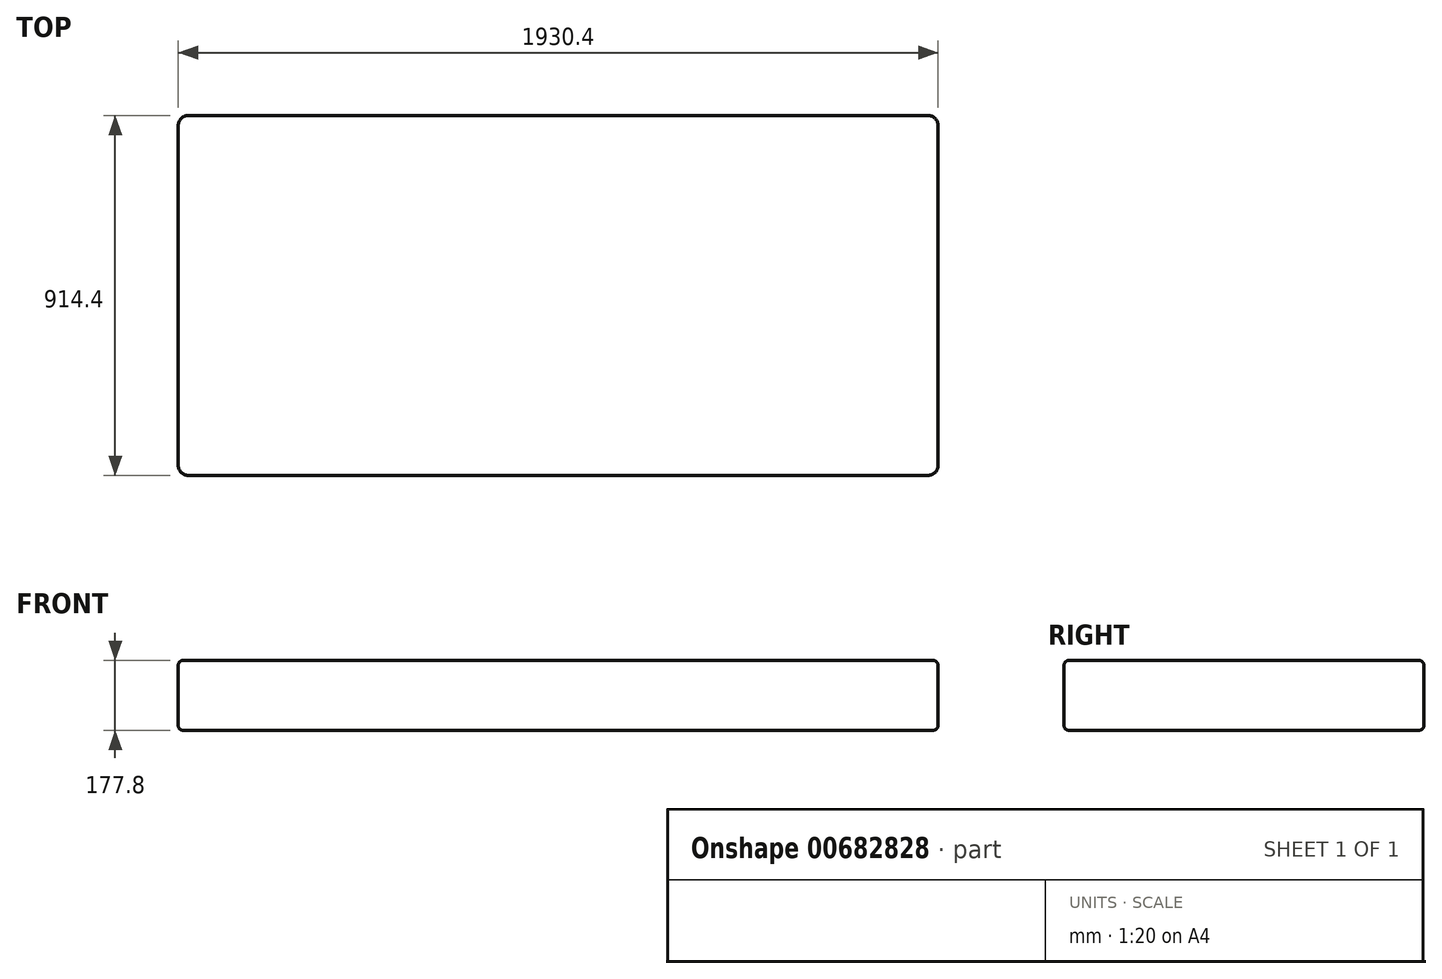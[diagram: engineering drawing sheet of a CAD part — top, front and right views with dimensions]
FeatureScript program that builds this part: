
annotation { "Feature Type Name" : "Feature", "Feature Type Description" : "" }
export const myFeature = defineFeature(function(context is Context, id is Id, definition is map)
    precondition{}
    {
        {
            var Q0;
            Q0=qCreatedBy(makeId("Top.planeOp"),FACE);
            var sketch = newSketch(context, id + "F0", { "sketchPlane" : qUnion([Q0])});
            skLineSegment(sketch, "E0.bottom", {"start": v(0, 0) * mm, "end": v(-1930.4, 0) * mm});
            skLineSegment(sketch, "E0.top", {"start": v(0, 914.4) * mm, "end": v(-1930.4, 914.4) * mm});
            skLineSegment(sketch, "E0.left", {"start": v(0, 0) * mm, "end": v(0, 914.4) * mm});
            skLineSegment(sketch, "E0.right", {"start": v(-1930.4, 0) * mm, "end": v(-1930.4, 914.4) * mm});
            skSolve(sketch);
        }
        {
            var Q0;
            Q0=makeQuery(id+"F0.imprint","IMPRINT",FACE,{"disambiguationData":[TD([[makeQuery(id+"F0.imprint","IMPRINT",EDGE,{"derivedFrom":sQuery(id+"F0.wireOp",EDGE,"E0.bottom")}),-1.0]])]});
            extrude(context, id + "F1", {"entities" : qUnion([Q0]), "depth" : 177.8 * mm, "offsetDistance" : 25.4 * mm});
        }
        {
            var Q0;
            Q0=makeQuery(id+"F1.opExtrude","CAP_FACE",FACE,{"disambiguationData":[OSD([sQuery(id+"F0.wireOp",EDGE,"E0.bottom"),sQuery(id+"F0.wireOp",EDGE,"E0.top"),sQuery(id+"F0.wireOp",EDGE,"E0.left"),sQuery(id+"F0.wireOp",EDGE,"E0.right")])],"isStart":false});
            fillet(context, id + "F2", {"entities" : qUnion([Q0]), "radius" : 12.7 * mm, "tangentPropagation" : true, "allowEdgeOverflow" : false});
        }
        {
            var Q0;
            Q0=makeQuery(id+"F1.opExtrude","CAP_FACE",FACE,{"disambiguationData":[OSD([sQuery(id+"F0.wireOp",EDGE,"E0.bottom"),sQuery(id+"F0.wireOp",EDGE,"E0.top"),sQuery(id+"F0.wireOp",EDGE,"E0.left"),sQuery(id+"F0.wireOp",EDGE,"E0.right")])],"isStart":true});
            fillet(context, id + "F3", {"entities" : qUnion([Q0]), "radius" : 12.7 * mm, "tangentPropagation" : true, "allowEdgeOverflow" : false});
        }
        {
            var Q0;
            Q0=makeQuery(id+"F1.opExtrude","SWEPT_EDGE",EDGE,{"disambiguationData":[OSD([sQuery(id+"F0.wireOp",EDGE,"E0.top"),sQuery(id+"F0.wireOp",EDGE,"E0.right")])]});
            var Q1;
            Q1=makeQuery(id+"F1.opExtrude","SWEPT_EDGE",EDGE,{"disambiguationData":[OSD([sQuery(id+"F0.wireOp",EDGE,"E0.bottom"),sQuery(id+"F0.wireOp",EDGE,"E0.right")])]});
            var Q2;
            Q2=makeQuery(id+"F1.opExtrude","SWEPT_EDGE",EDGE,{"disambiguationData":[OSD([sQuery(id+"F0.wireOp",EDGE,"E0.bottom"),sQuery(id+"F0.wireOp",EDGE,"E0.left")])]});
            var Q3;
            Q3=makeQuery(id+"F1.opExtrude","SWEPT_EDGE",EDGE,{"disambiguationData":[OSD([sQuery(id+"F0.wireOp",EDGE,"E0.top"),sQuery(id+"F0.wireOp",EDGE,"E0.left")])]});
            fillet(context, id + "F4", {"entities" : qUnion([Q0, Q1, Q2, Q3]), "radius" : 25.4 * mm, "tangentPropagation" : true, "allowEdgeOverflow" : false});
        }
    });
